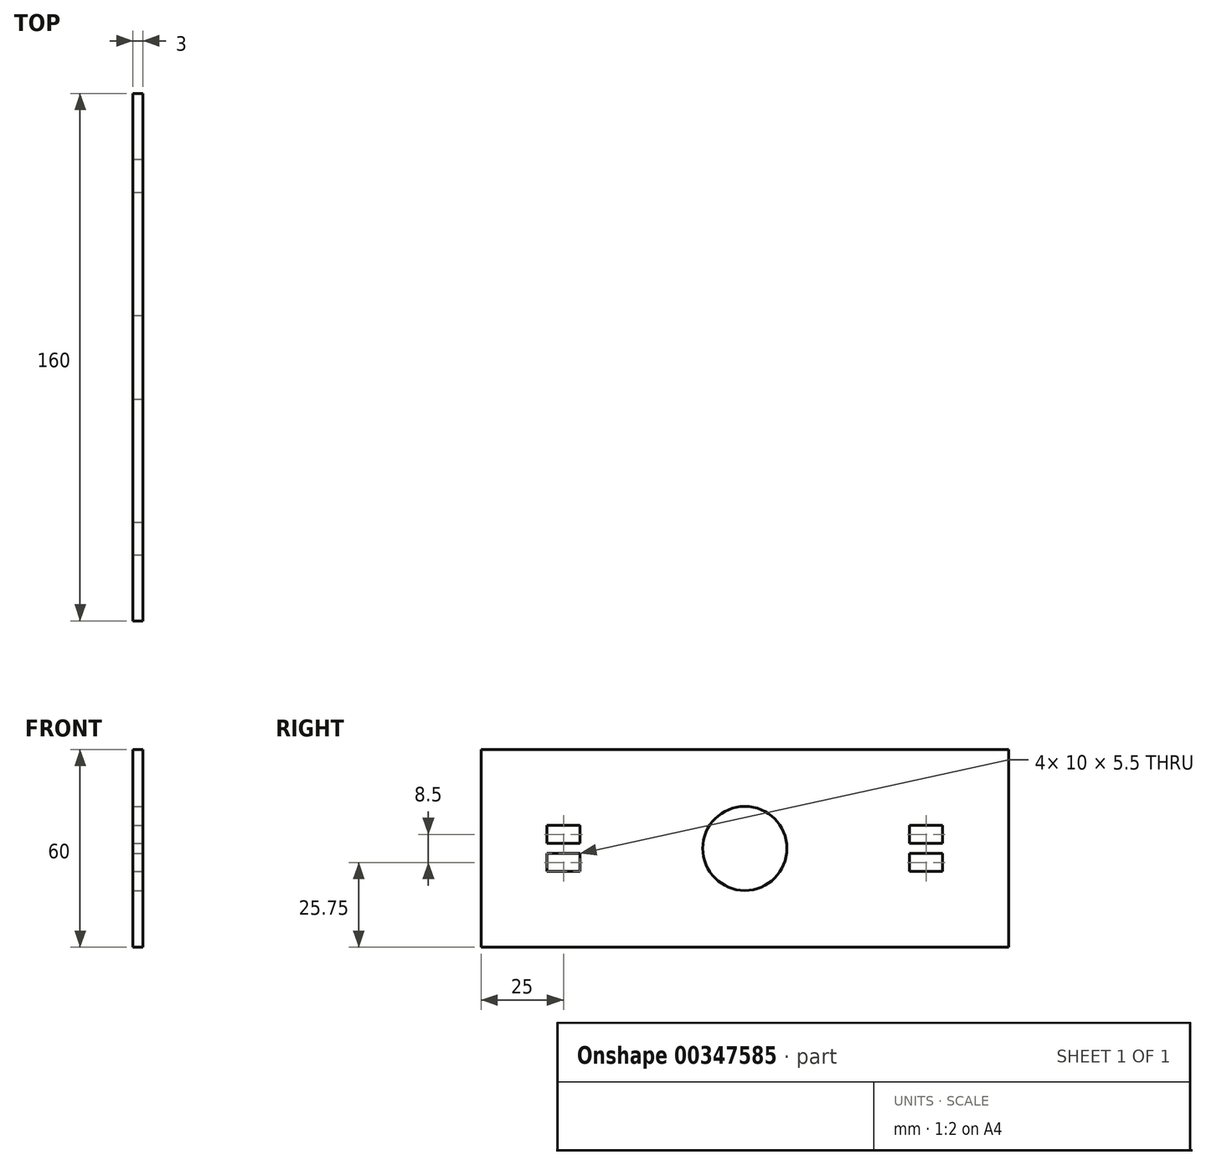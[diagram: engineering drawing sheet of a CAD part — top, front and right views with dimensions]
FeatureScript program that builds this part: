
annotation { "Feature Type Name" : "Feature", "Feature Type Description" : "" }
export const myFeature = defineFeature(function(context is Context, id is Id, definition is map)
    precondition{}
    {
        {
            var Q0;
            Q0=qCreatedBy(makeId("Right.planeOp"),FACE);
            var sketch = newSketch(context, id + "F0", { "sketchPlane" : qUnion([Q0])});
            skLineSegment(sketch, "E0", {"start": v(0, 30) * mm, "end": v(80, 30) * mm});
            skLineSegment(sketch, "E1", {"start": v(80, 30) * mm, "end": v(80, -30) * mm});
            skLineSegment(sketch, "E2", {"start": v(80, -30) * mm, "end": v(0, -30) * mm});
            skLineSegment(sketch, "E3.MirrorCS", {"start": v(0, 30) * mm, "end": v(-80, 30) * mm});
            skLineSegment(sketch, "E4.MirrorCS", {"start": v(-80, 30) * mm, "end": v(-80, -30) * mm});
            skLineSegment(sketch, "E5.MirrorCS", {"start": v(-80, -30) * mm, "end": v(0, -30) * mm});
            skSolve(sketch);
        }
        {
            var Q0;
            Q0=makeQuery(id+"F0.imprint","IMPRINT",FACE,{"disambiguationData":[TD([[makeQuery(id+"F0.imprint","IMPRINT",EDGE,{"derivedFrom":sQuery(id+"F0.wireOp",EDGE,"E0")}),-1.0]])]});
            extrude(context, id + "F1", {"entities" : qUnion([Q0]), "depth" : 3 * mm});
        }
        {
            var Q0;
            Q0=makeQuery(id+"F1.opExtrude","CAP_FACE",FACE,{"disambiguationData":[OSD([sQuery(id+"F0.wireOp",EDGE,"E0"),sQuery(id+"F0.wireOp",EDGE,"E1"),sQuery(id+"F0.wireOp",EDGE,"E2"),sQuery(id+"F0.wireOp",EDGE,"E3.MirrorCS"),sQuery(id+"F0.wireOp",EDGE,"E4.MirrorCS"),sQuery(id+"F0.wireOp",EDGE,"E5.MirrorCS")])],"isStart":false});
            var sketch = newSketch(context, id + "F2", { "sketchPlane" : qUnion([Q0])});
            skLineSegment(sketch, "E6.bottom", {"start": v(-60, 7) * mm, "end": v(-50, 7) * mm});
            skLineSegment(sketch, "E6.top", {"start": v(-60, 1.5) * mm, "end": v(-50, 1.5) * mm});
            skLineSegment(sketch, "E6.left", {"start": v(-60, 7) * mm, "end": v(-60, 1.5) * mm});
            skLineSegment(sketch, "E6.right", {"start": v(-50, 7) * mm, "end": v(-50, 1.5) * mm});
            skLineSegment(sketch, "E7.MirrorCS", {"start": v(-60, -1.5) * mm, "end": v(-50, -1.5) * mm});
            skLineSegment(sketch, "E8.MirrorCS", {"start": v(-60, -7) * mm, "end": v(-60, -1.5) * mm});
            skLineSegment(sketch, "E9.MirrorCS", {"start": v(-60, -7) * mm, "end": v(-50, -7) * mm});
            skLineSegment(sketch, "E10.MirrorCS", {"start": v(-50, -7) * mm, "end": v(-50, -1.5) * mm});
            skLineSegment(sketch, "E11.MirrorCS", {"start": v(60, 7) * mm, "end": v(60, 1.5) * mm});
            skLineSegment(sketch, "E12.MirrorCS", {"start": v(60, 7) * mm, "end": v(50, 7) * mm});
            skLineSegment(sketch, "E13.MirrorCS", {"start": v(50, 7) * mm, "end": v(50, 1.5) * mm});
            skLineSegment(sketch, "E14.MirrorCS", {"start": v(60, 1.5) * mm, "end": v(50, 1.5) * mm});
            skLineSegment(sketch, "E15.MirrorCS", {"start": v(60, -1.5) * mm, "end": v(50, -1.5) * mm});
            skLineSegment(sketch, "E16.MirrorCS", {"start": v(60, -7) * mm, "end": v(60, -1.5) * mm});
            skLineSegment(sketch, "E17.MirrorCS", {"start": v(60, -7) * mm, "end": v(50, -7) * mm});
            skLineSegment(sketch, "E18.MirrorCS", {"start": v(50, -7) * mm, "end": v(50, -1.5) * mm});
            skSolve(sketch);
        }
        {
            var Q0;
            Q0=makeQuery(id+"F2.imprint","IMPRINT",FACE,{"disambiguationData":[TD([[makeQuery(id+"F2.imprint","IMPRINT",EDGE,{"derivedFrom":sQuery(id+"F2.wireOp",EDGE,"E7.MirrorCS")}),-1.0]])]});
            var Q1;
            Q1=makeQuery(id+"F2.imprint","IMPRINT",FACE,{"disambiguationData":[TD([[makeQuery(id+"F2.imprint","IMPRINT",EDGE,{"derivedFrom":sQuery(id+"F2.wireOp",EDGE,"E6.bottom")}),-1.0]])]});
            var Q2;
            Q2=makeQuery(id+"F2.imprint","IMPRINT",FACE,{"disambiguationData":[TD([[makeQuery(id+"F2.imprint","IMPRINT",EDGE,{"derivedFrom":sQuery(id+"F2.wireOp",EDGE,"E11.MirrorCS")}),-1.0]])]});
            var Q3;
            Q3=makeQuery(id+"F2.imprint","IMPRINT",FACE,{"disambiguationData":[TD([[makeQuery(id+"F2.imprint","IMPRINT",EDGE,{"derivedFrom":sQuery(id+"F2.wireOp",EDGE,"E15.MirrorCS")}),1.0]])]});
            extrude(context, id + "F3", {"entities" : qUnion([Q0, Q1, Q2, Q3]), "operationType" : NewBodyOperationType.REMOVE, "oppositeDirection" : true, "depth" : 25 * mm});
        }
        {
            var Q0;
            Q0=makeQuery(id+"F1.opExtrude","CAP_FACE",FACE,{"disambiguationData":[OSD([sQuery(id+"F0.wireOp",EDGE,"E0"),sQuery(id+"F0.wireOp",EDGE,"E1"),sQuery(id+"F0.wireOp",EDGE,"E2"),sQuery(id+"F0.wireOp",EDGE,"E3.MirrorCS"),sQuery(id+"F0.wireOp",EDGE,"E4.MirrorCS"),sQuery(id+"F0.wireOp",EDGE,"E5.MirrorCS")])],"isStart":false});
            var sketch = newSketch(context, id + "F4", { "sketchPlane" : qUnion([Q0])});
            skCircle(sketch, "E19", {"center": v(0, 0) * mm, "radius": 12.75 * mm});
            skSolve(sketch);
        }
        {
            var Q0;
            Q0=makeQuery(id+"F4.imprint","IMPRINT",FACE,{"disambiguationData":[TD([[makeQuery(id+"F4.imprint","IMPRINT",EDGE,{"derivedFrom":sQuery(id+"F4.wireOp",EDGE,"E19")}),1.0]])]});
            extrude(context, id + "F5", {"entities" : qUnion([Q0]), "operationType" : NewBodyOperationType.REMOVE, "oppositeDirection" : true, "depth" : 25 * mm});
        }
    });
